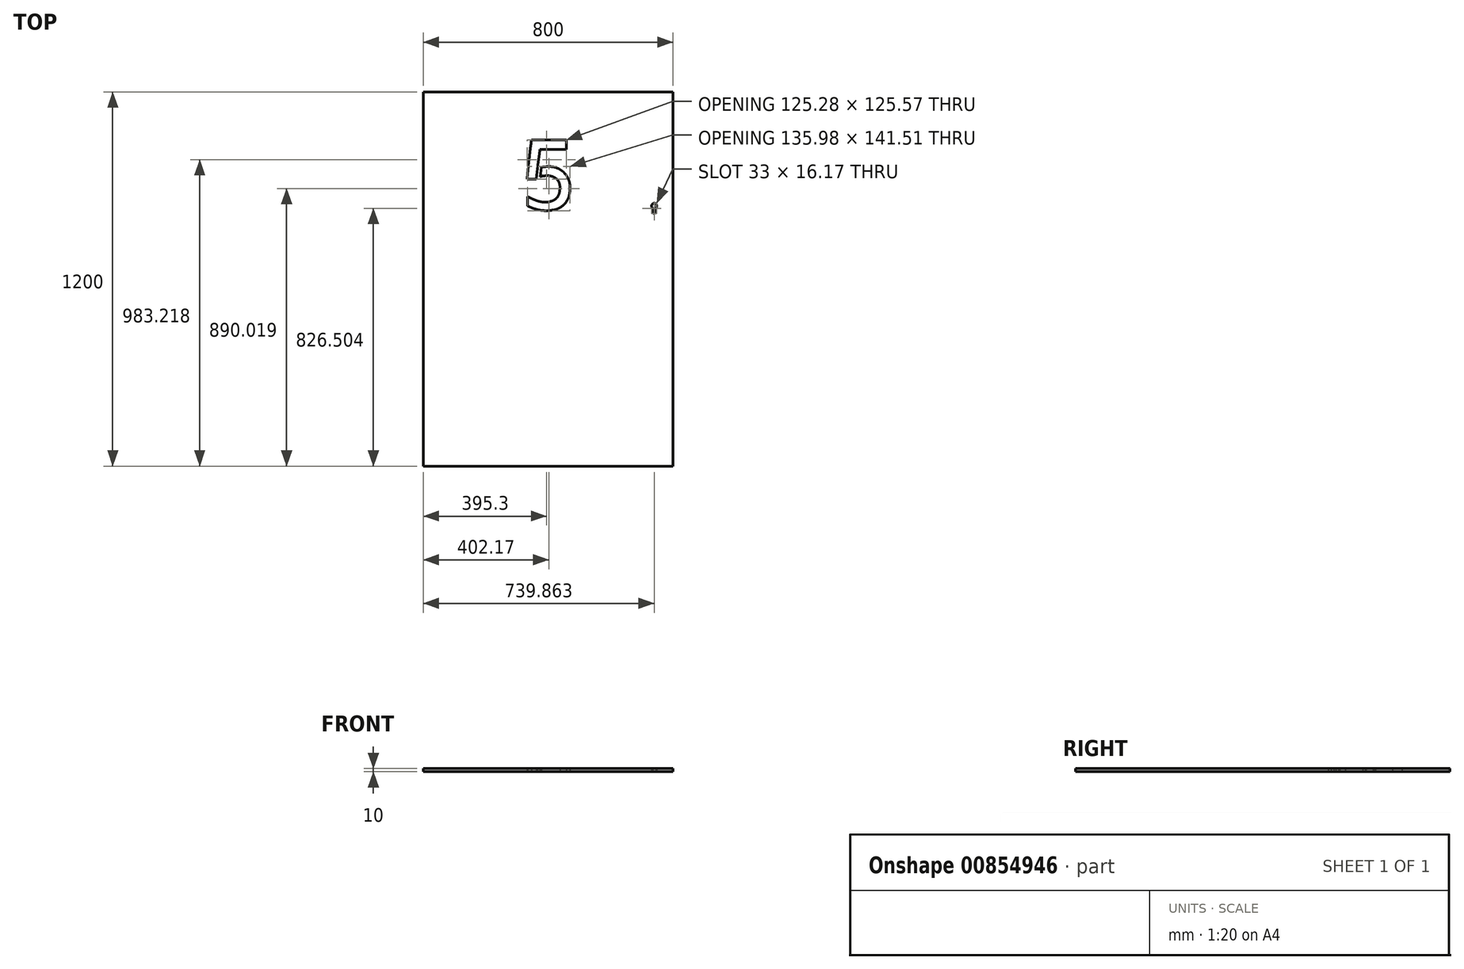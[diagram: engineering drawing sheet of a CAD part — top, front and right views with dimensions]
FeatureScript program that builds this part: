
annotation { "Feature Type Name" : "Feature", "Feature Type Description" : "" }
export const myFeature = defineFeature(function(context is Context, id is Id, definition is map)
    precondition{}
    {
        {
            var Q0;
            Q0=qCreatedBy(makeId("Top.planeOp"),FACE);
            var sketch = newSketch(context, id + "F0", { "sketchPlane" : qUnion([Q0])});
            skLineSegment(sketch, "E0.bottom", {"start": v(400, -628.04) * mm, "end": v(-400, -628.04) * mm});
            skLineSegment(sketch, "E0.top", {"start": v(400, 571.96) * mm, "end": v(-400, 571.96) * mm});
            skLineSegment(sketch, "E0.left", {"start": v(400, -628.04) * mm, "end": v(400, 571.96) * mm});
            skLineSegment(sketch, "E0.right", {"start": v(-400, -628.04) * mm, "end": v(-400, 571.96) * mm});
            skLineSegment(sketch, "E1", {"start": v(-400, 571.96) * mm, "end": v(-400, 521.96) * mm});
            skLineSegment(sketch, "E2", {"start": v(350, -628.04) * mm, "end": v(-350, -628.04) * mm});
            skText(sketch, "E3", { "text": "5", "fontName": "AllertaStencil-Regular.ttf"});
            skLineSegment(sketch, "E4", {"start": v(400, -628.04) * mm, "end": v(400, 171.96) * mm});
            skLineSegment(sketch, "E5", {"start": v(400, 171.96) * mm, "end": v(306, 171.96) * mm});
            skLineSegment(sketch, "E6", {"start": v(306, 171.96) * mm, "end": v(306, 344.96) * mm});
            skLineSegment(sketch, "E7", {"start": v(306, 344.96) * mm, "end": v(400, 344.96) * mm});
            skLineSegment(sketch, "E8", {"start": v(400, 171.96) * mm, "end": v(340, 171.96) * mm});
            skArc(sketch, "E9", {"start": v(344.86, 199.6) * mm, "mid": v(339.86, 214.96) * mm, "end": v(334.86, 199.6) * mm});
            skArc(sketch, "E10", {"start": v(334.86, 186.96) * mm, "mid": v(339.86, 181.96) * mm, "end": v(344.86, 186.96) * mm});
            skLineSegment(sketch, "E11", {"start": v(334.86, 186.96) * mm, "end": v(334.86, 199.6) * mm});
            skLineSegment(sketch, "E12", {"start": v(344.86, 186.96) * mm, "end": v(344.86, 199.6) * mm});
            skCircle(sketch, "E13", {"center": v(339.86, 278.46) * mm, "radius": 10 * mm});
            skLineSegment(sketch, "E14.bottom", {"start": v(335.36, 273.96) * mm, "end": v(344.36, 273.96) * mm});
            skLineSegment(sketch, "E14.top", {"start": v(335.36, 282.96) * mm, "end": v(344.36, 282.96) * mm});
            skLineSegment(sketch, "E14.left", {"start": v(335.36, 273.96) * mm, "end": v(335.36, 282.96) * mm});
            skLineSegment(sketch, "E14.right", {"start": v(344.36, 273.96) * mm, "end": v(344.36, 282.96) * mm});
            skLineSegment(sketch, "E15", {"start": v(339.86, 181.96) * mm, "end": v(340, 171.96) * mm});
            const initialGuessF0  = {"E3": [-0.0912, 0.19274, 1, 0, 0.22532]};
            skSetInitialGuess(sketch, initialGuessF0);
            skSolve(sketch);
        }
        {
            var Q0;
            Q0=makeQuery(id+"F0.imprint","IMPRINT",FACE,{"disambiguationData":[TD([[makeQuery(id+"F0.imprint","IMPRINT",EDGE,{"derivedFrom":sQuery(id+"F0.wireOp",EDGE,"E0.bottom")}),-1.0]])]});
            var Q1;
            Q1=makeQuery(id+"F0.imprint","IMPRINT",FACE,{"disambiguationData":[TD([[makeQuery(id+"F0.imprint","IMPRINT",EDGE,{"derivedFrom":sQuery(id+"F0.wireOp",EDGE,"E5")}),-1.0]])]});
            var Q2;
            Q2=makeQuery(id+"F0.imprint","IMPRINT",FACE,{"disambiguationData":[TD([[makeQuery(id+"F0.imprint","IMPRINT",EDGE,{"derivedFrom":sQuery(id+"F0.wireOp",EDGE,"E14.bottom")}),1.0]])]});
            var Q3;
            Q3=makeQuery(id+"F0.imprint","IMPRINT",FACE,{"disambiguationData":[TD([[makeQuery(id+"F0.imprint","IMPRINT",EDGE,{"derivedFrom":sQuery(id+"F0.wireOp",EDGE,"E13")}),1.0]])]});
            extrude(context, id + "F1", {"entities" : qUnion([Q0, Q1, Q2, Q3]), "depth" : 10 * mm, "offsetDistance" : 25 * mm});
        }
    });
